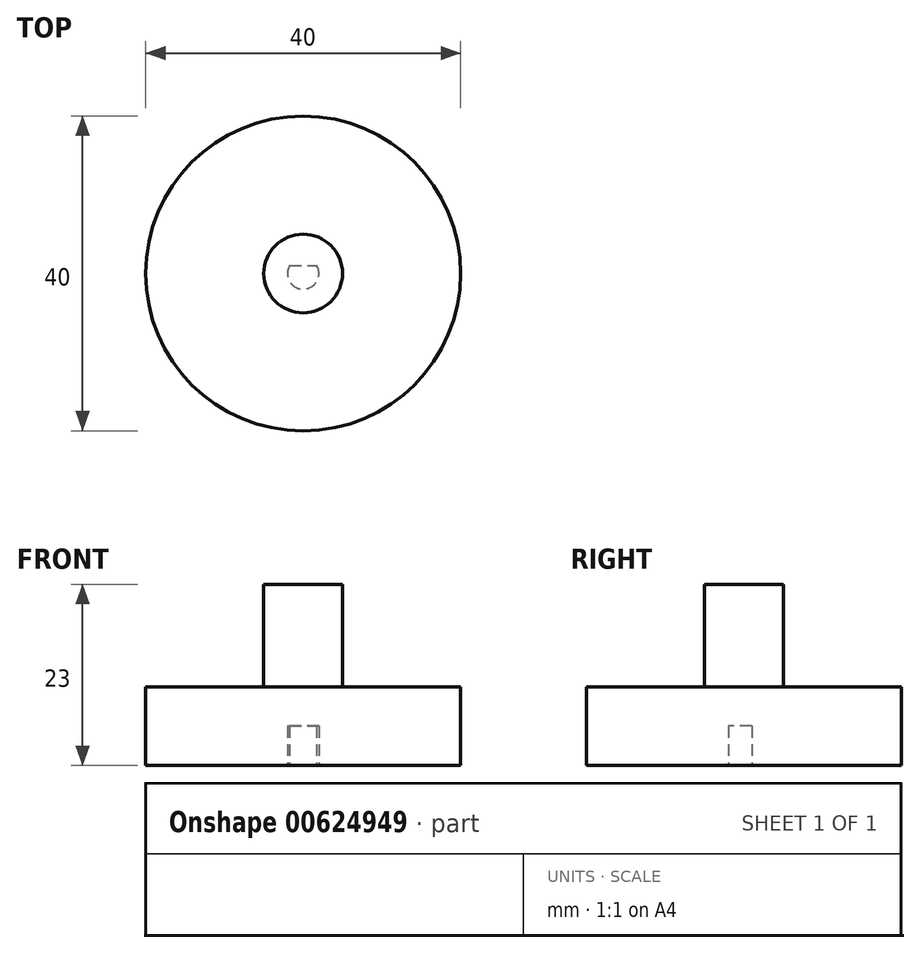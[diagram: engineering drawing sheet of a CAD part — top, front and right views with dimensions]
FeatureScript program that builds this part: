
annotation { "Feature Type Name" : "Feature", "Feature Type Description" : "" }
export const myFeature = defineFeature(function(context is Context, id is Id, definition is map)
    precondition{}
    {
        {
            var Q0;
            Q0=qCreatedBy(makeId("Top.planeOp"),FACE);
            var sketch = newSketch(context, id + "F0", { "sketchPlane" : qUnion([Q0])});
            skCircle(sketch, "E0", {"center": v(0, 0) * mm, "radius": 20 * mm});
            skSolve(sketch);
        }
        {
            var Q0;
            Q0=makeQuery(id+"F0.imprint","IMPRINT",FACE,{"disambiguationData":[TD([[makeQuery(id+"F0.imprint","IMPRINT",EDGE,{"derivedFrom":sQuery(id+"F0.wireOp",EDGE,"E0")}),1.0]])]});
            extrude(context, id + "F1", {"entities" : qUnion([Q0]), "depth" : 10 * mm, "offsetDistance" : 25 * mm});
        }
        {
            var Q0;
            Q0=makeQuery(id+"F1.opExtrude","CAP_FACE",FACE,{"disambiguationData":[OSD([sQuery(id+"F0.wireOp",EDGE,"E0")])],"isStart":false});
            var sketch = newSketch(context, id + "F2", { "sketchPlane" : qUnion([Q0])});
            skCircle(sketch, "E1", {"center": v(0, 0) * mm, "radius": 5 * mm});
            skSolve(sketch);
        }
        {
            var Q0;
            Q0=makeQuery(id+"F2.imprint","IMPRINT",FACE,{"disambiguationData":[TD([[makeQuery(id+"F2.imprint","IMPRINT",EDGE,{"derivedFrom":sQuery(id+"F2.wireOp",EDGE,"E1")}),1.0]])]});
            extrude(context, id + "F3", {"entities" : qUnion([Q0]), "operationType" : NewBodyOperationType.ADD, "depth" : 13 * mm, "offsetDistance" : 25 * mm});
        }
        {
            var Q0;
            Q0=makeQuery(id+"F1.opExtrude","CAP_FACE",FACE,{"disambiguationData":[OSD([sQuery(id+"F0.wireOp",EDGE,"E0")])],"isStart":true});
            var sketch = newSketch(context, id + "F4", { "sketchPlane" : qUnion([Q0])});
            skArc(sketch, "E2", {"start": v(1.73, -1) * mm, "mid": v(0, 2) * mm, "end": v(-1.73, -1) * mm});
            skLineSegment(sketch, "E3", {"start": v(0, 2) * mm, "end": v(0, -1) * mm, "construction": true});
            skLineSegment(sketch, "E4", {"start": v(0, -1) * mm, "end": v(1.73, -1) * mm});
            skLineSegment(sketch, "E5", {"start": v(1.73, -1) * mm, "end": v(0, -1) * mm});
            skLineSegment(sketch, "E6", {"start": v(-1.73, -1) * mm, "end": v(0, -1) * mm});
            skPoint(sketch, "E7", {"position": v(-1.73, -1) * mm});
            skPoint(sketch, "E8", {"position": v(1.73, -1) * mm});
            skSolve(sketch);
        }
        {
            var Q0;
            Q0=makeQuery(id+"F4.imprint","IMPRINT",FACE,{"disambiguationData":[TD([[makeQuery(id+"F4.imprint","IMPRINT",EDGE,{"derivedFrom":sQuery(id+"F4.wireOp",EDGE,"E2")}),1.0]])]});
            extrude(context, id + "F5", {"entities" : qUnion([Q0]), "operationType" : NewBodyOperationType.REMOVE, "oppositeDirection" : true, "depth" : 5 * mm, "offsetDistance" : 25 * mm});
        }
    });
